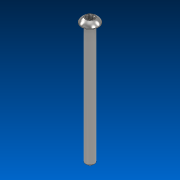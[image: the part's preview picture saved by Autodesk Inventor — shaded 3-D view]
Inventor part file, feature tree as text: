
AUTODESK INVENTOR PART (.ipt)
format: ipt  version: 2022.2 (Build 262287000, 287)  size: 150,528 bytes
history: native  units: in
note: dims shown in document units (in); Inventor stores cm internally (conversion verified against a paired STEP export)
features: chamfer x1
ambient origin geometry x8: Origin, YZ Plane, XZ Plane, XY Plane, X Axis, Y Axis, Z Axis, Center Point
bodies: Solid1 (feature_tree)
feature tree (1):
  chamfer  "Chamfer2"  [1 undecoded]
note: 1 required parameter value undecoded (feature->parameter linkage not recoverable at this tier; creation-order binding heuristic only, values carry confidence <= 0.55)
